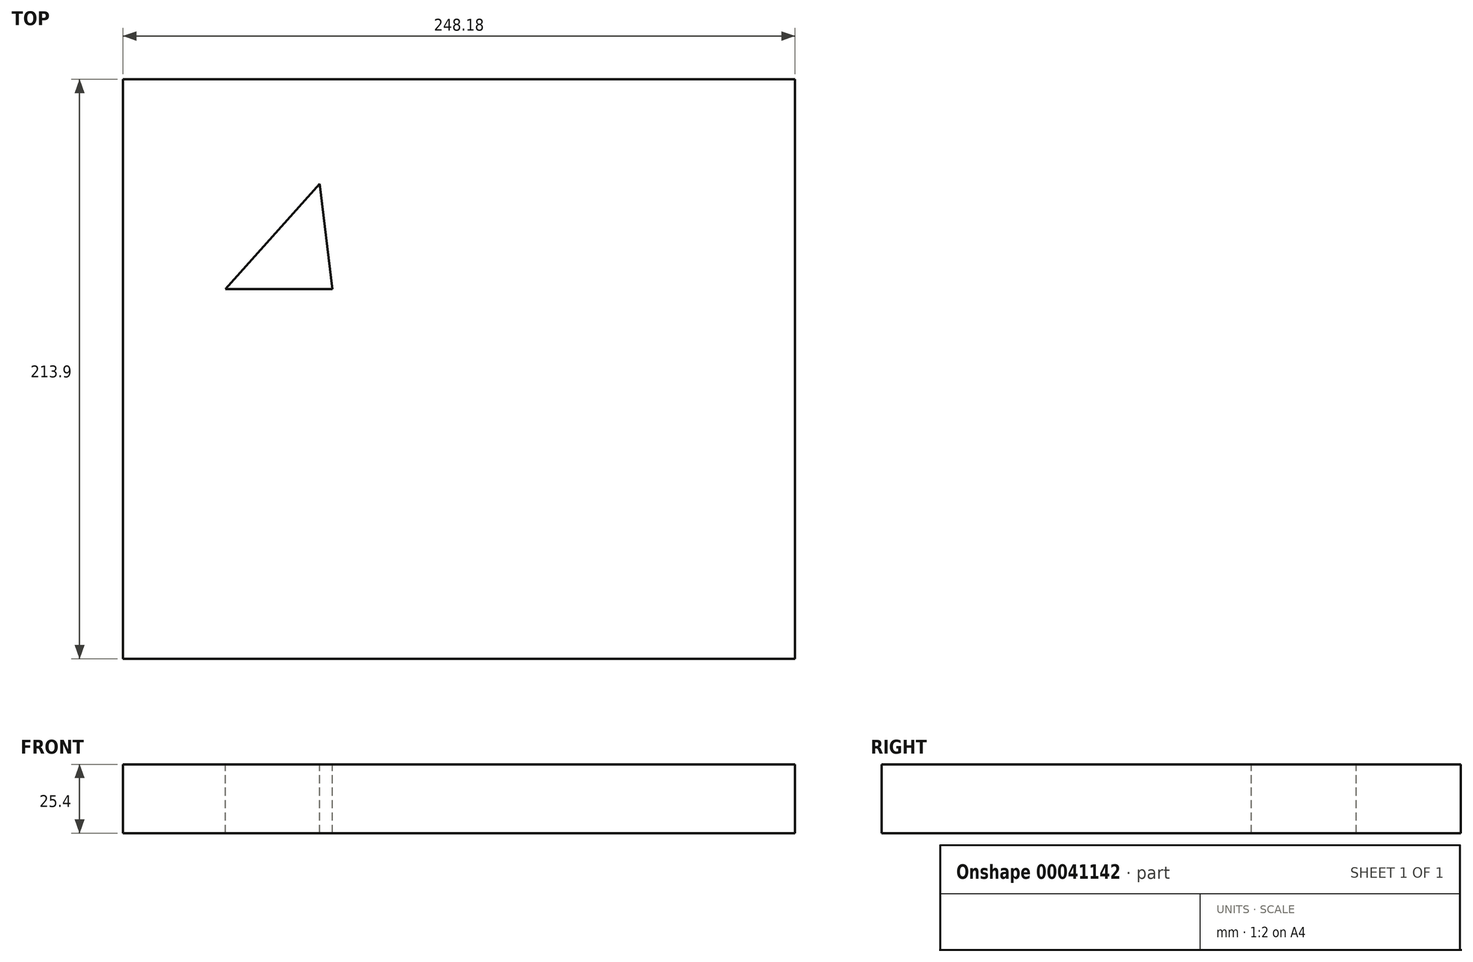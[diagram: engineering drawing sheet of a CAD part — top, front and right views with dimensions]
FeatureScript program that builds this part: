
annotation { "Feature Type Name" : "Feature", "Feature Type Description" : "" }
export const myFeature = defineFeature(function(context is Context, id is Id, definition is map)
    precondition{}
    {
        {
            var Q0;
            Q0=qCreatedBy(makeId("Top.planeOp"),FACE);
            var sketch = newSketch(context, id + "F0", { "sketchPlane" : qUnion([Q0])});
            skLineSegment(sketch, "E0.rect.bottom", {"start": v(124.1, 106.95) * mm, "end": v(-124.1, 106.95) * mm});
            skLineSegment(sketch, "E0.rect.top", {"start": v(124.1, -106.95) * mm, "end": v(-124.1, -106.95) * mm});
            skLineSegment(sketch, "E0.rect.left", {"start": v(124.1, 106.95) * mm, "end": v(124.1, -106.95) * mm});
            skLineSegment(sketch, "E0.rect.right", {"start": v(-124.1, 106.95) * mm, "end": v(-124.1, -106.95) * mm});
            skPoint(sketch, "E0.rect.middle", {"position": v(0, 0) * mm});
            skSolve(sketch);
        }
        {
            var Q0;
            Q0 = qSketchRegion(id + "F0", true);
            extrude(context, id + "F1", {"entities" : qUnion([Q0]), "endBound" : BoundingType.SYMMETRIC, "depth" : 25.4 * mm});
        }
        {
            var Q0;
            Q0=makeQuery(id+"F1.opExtrude","CAP_FACE",FACE,{"disambiguationData":[OSD([sQuery(id+"F0.wireOp",EDGE,"E0.rect.bottom"),sQuery(id+"F0.wireOp",EDGE,"E0.rect.top"),sQuery(id+"F0.wireOp",EDGE,"E0.rect.left"),sQuery(id+"F0.wireOp",EDGE,"E0.rect.right")])],"isStart":false});
            var sketch = newSketch(context, id + "F2", { "sketchPlane" : qUnion([Q0])});
            skLineSegment(sketch, "E1", {"start": v(-51.5, 68.32) * mm, "end": v(-86.25, 29.5) * mm});
            skLineSegment(sketch, "E2", {"start": v(-86.25, 29.5) * mm, "end": v(-46.74, 29.5) * mm});
            skLineSegment(sketch, "E3", {"start": v(-46.74, 29.5) * mm, "end": v(-51.5, 68.32) * mm});
            skSolve(sketch);
        }
        {
            var Q0;
            Q0=makeQuery(id+"F2.imprint","IMPRINT",FACE,{"disambiguationData":[TD([[makeQuery(id+"F2.imprint","IMPRINT",EDGE,{"derivedFrom":sQuery(id+"F2.wireOp",EDGE,"E1")}),1.0]])]});
            extrude(context, id + "F3", {"entities" : qUnion([Q0]), "oppositeDirection" : true, "depth" : 25.4 * mm});
        }
    });
